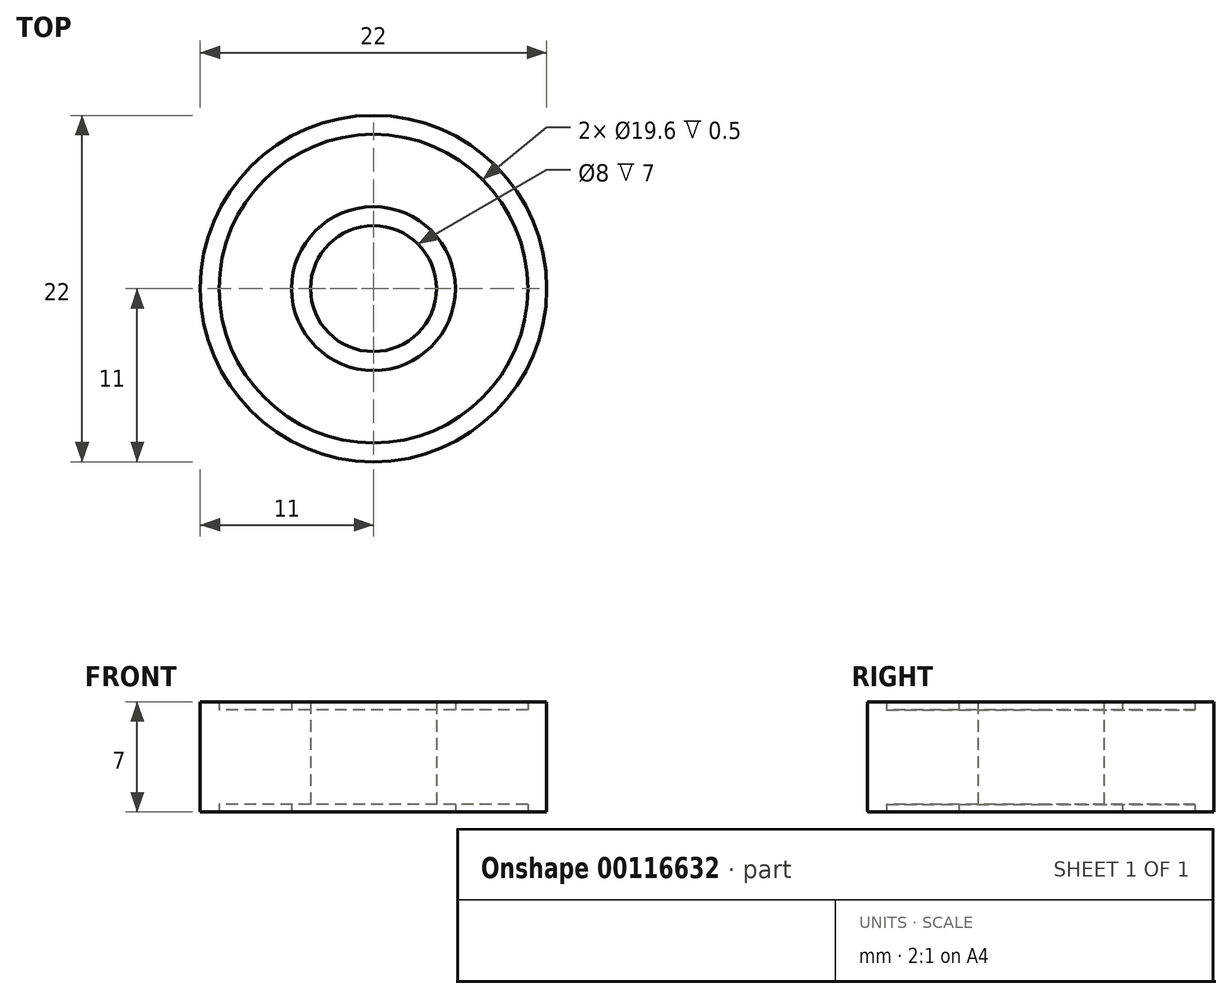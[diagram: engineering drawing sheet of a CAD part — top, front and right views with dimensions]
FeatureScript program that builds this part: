
annotation { "Feature Type Name" : "Feature", "Feature Type Description" : "" }
export const myFeature = defineFeature(function(context is Context, id is Id, definition is map)
    precondition{}
    {
        {
            assignVariable(context, id + "F0", {"name" : "Height", "anyValue" : 7});
        }
        {
            var Q0;
            Q0=qCreatedBy(makeId("Top.planeOp"),FACE);
            var sketch = newSketch(context, id + "F1", { "sketchPlane" : qUnion([Q0])});
            skCircle(sketch, "E0", {"center": v(0, 0) * mm, "radius": 4 * mm});
            skCircle(sketch, "E1", {"center": v(0, 0) * mm, "radius": 5.2 * mm});
            skCircle(sketch, "E2", {"center": v(0, 0) * mm, "radius": 9.8 * mm});
            skCircle(sketch, "E3", {"center": v(0, 0) * mm, "radius": 11 * mm});
            skSolve(sketch);
        }
        {
            var Q0;
            Q0=makeQuery(id+"F1.imprint","IMPRINT",FACE,{"disambiguationData":[TD([[makeQuery(id+"F1.imprint","IMPRINT",EDGE,{"derivedFrom":sQuery(id+"F1.wireOp",EDGE,"E2")}),-1.0]])]});
            var Q1;
            Q1=makeQuery(id+"F1.imprint","IMPRINT",FACE,{"disambiguationData":[TD([[makeQuery(id+"F1.imprint","IMPRINT",EDGE,{"derivedFrom":sQuery(id+"F1.wireOp",EDGE,"E0")}),-1.0]])]});
            extrude(context, id + "F2", {"entities" : qUnion([Q0, Q1]), "endBound" : BoundingType.SYMMETRIC, "depth" : (getVariable(context, 'Height')) * mm});
        }
        {
            var Q0;
            Q0=makeQuery(id+"F1.imprint","IMPRINT",FACE,{"disambiguationData":[TD([[makeQuery(id+"F1.imprint","IMPRINT",EDGE,{"derivedFrom":sQuery(id+"F1.wireOp",EDGE,"E1")}),-1.0]])]});
            extrude(context, id + "F3", {"entities" : qUnion([Q0]), "operationType" : NewBodyOperationType.ADD, "endBound" : BoundingType.SYMMETRIC, "depth" : (getVariable(context, 'Height') - 1) * mm});
        }
    });
